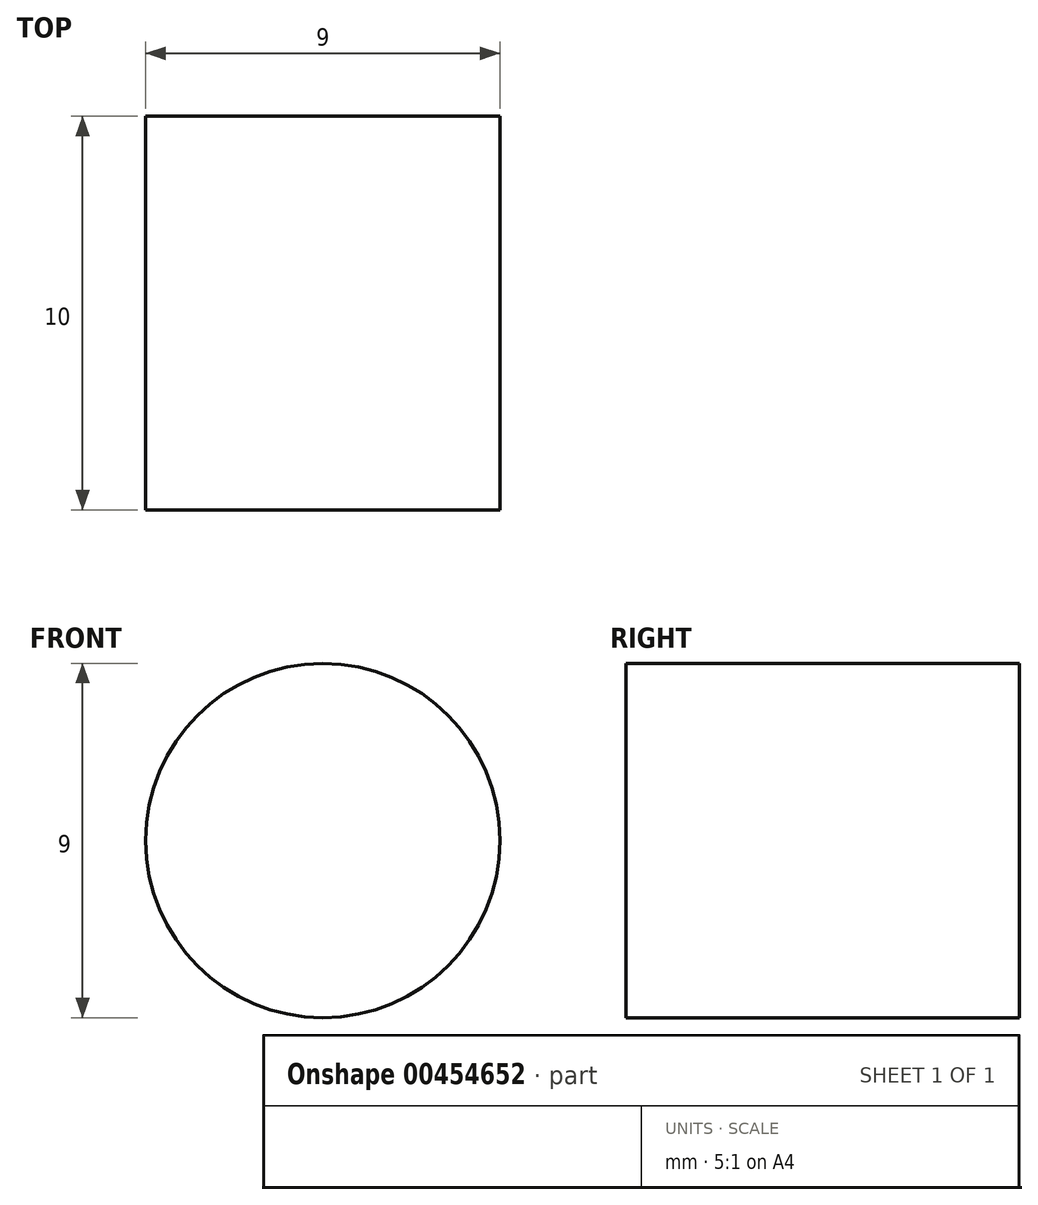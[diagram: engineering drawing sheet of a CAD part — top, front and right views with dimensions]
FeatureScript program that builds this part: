
annotation { "Feature Type Name" : "Feature", "Feature Type Description" : "" }
export const myFeature = defineFeature(function(context is Context, id is Id, definition is map)
    precondition{}
    {
        {
            var Q0;
            Q0=qCreatedBy(makeId("Front.planeOp"),FACE);
            var sketch = newSketch(context, id + "F0", { "sketchPlane" : qUnion([Q0])});
            skCircle(sketch, "E0", {"center": v(0, 0) * mm, "radius": 4.5 * mm});
            skSolve(sketch);
        }
        {
            var Q0;
            Q0 = qSketchRegion(id + "F0", true);
            extrude(context, id + "F1", {"entities" : qUnion([Q0]), "depth" : 10 * mm, "offsetDistance" : 25 * mm});
        }
    });
